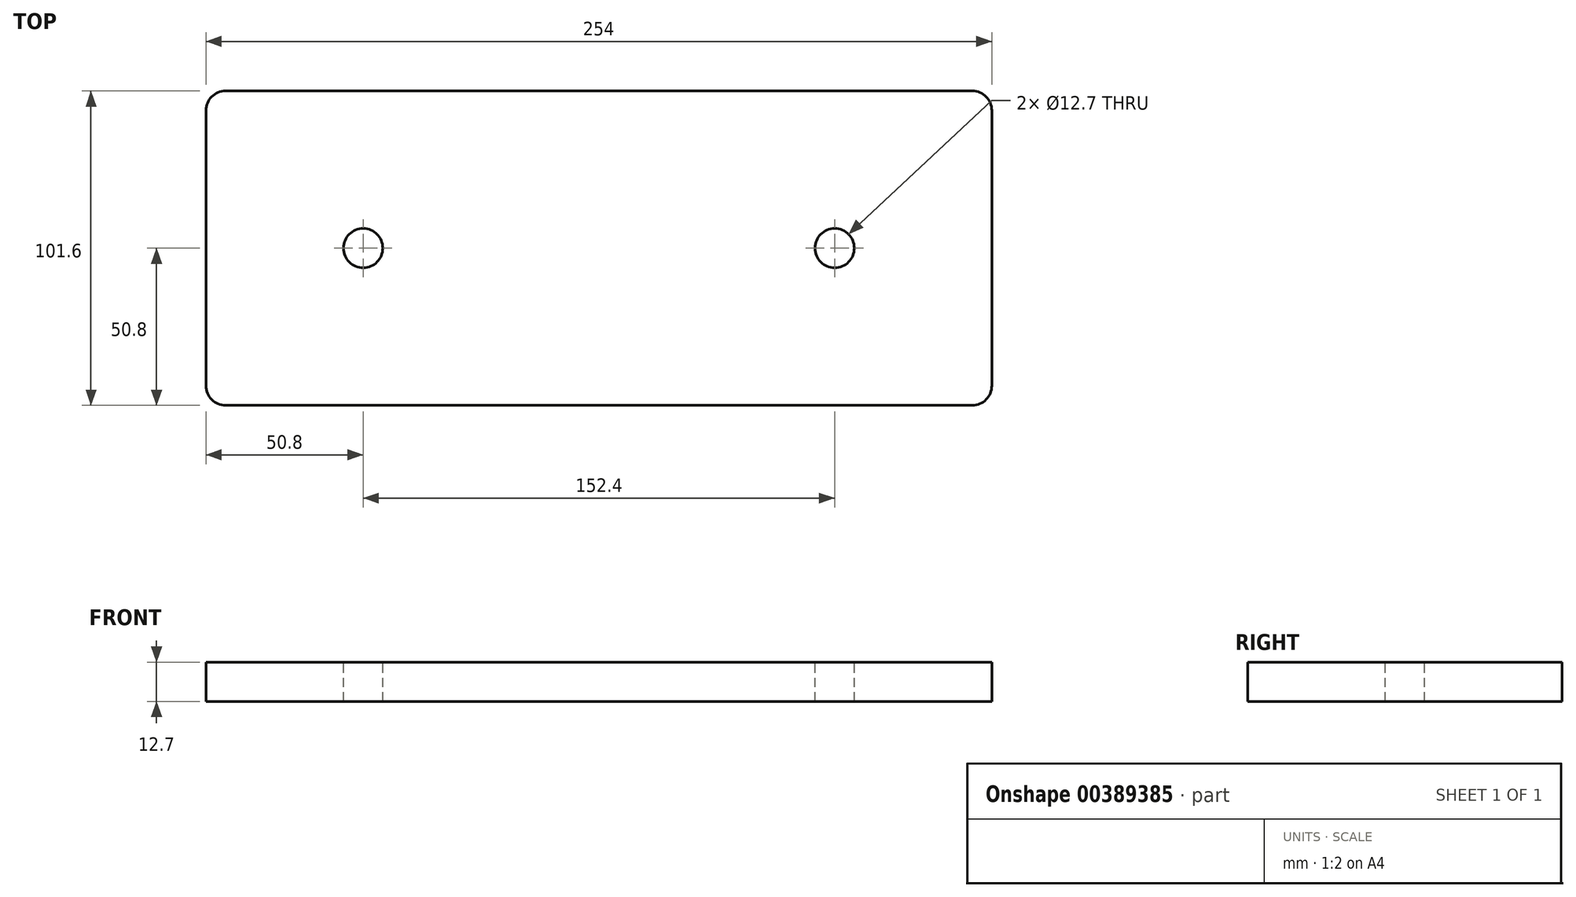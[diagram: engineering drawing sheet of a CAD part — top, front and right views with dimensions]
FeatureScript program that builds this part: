
annotation { "Feature Type Name" : "Feature", "Feature Type Description" : "" }
export const myFeature = defineFeature(function(context is Context, id is Id, definition is map)
    precondition{}
    {
        {
            var Q0;
            Q0=qCreatedBy(makeId("Top.planeOp"),FACE);
            var sketch = newSketch(context, id + "F0", { "sketchPlane" : qUnion([Q0])});
            skLineSegment(sketch, "E0.bottom", {"start": v(6.35, 0) * mm, "end": v(247.65, 0) * mm});
            skLineSegment(sketch, "E0.top", {"start": v(6.35, 101.6) * mm, "end": v(247.65, 101.6) * mm});
            skLineSegment(sketch, "E0.left", {"start": v(0, 6.35) * mm, "end": v(0, 95.25) * mm});
            skLineSegment(sketch, "E0.right", {"start": v(254, 6.35) * mm, "end": v(254, 95.25) * mm});
            skPoint(sketch, "E1.visualSharp", {"position": v(0, 101.6) * mm});
            skArc(sketch, "E1.filletArc", {"start": v(6.35, 101.6) * mm, "mid": v(1.86, 99.74) * mm, "end": v(0, 95.25) * mm});
            skPoint(sketch, "E2.visualSharp", {"position": v(0, 0) * mm});
            skArc(sketch, "E2.filletArc", {"start": v(0, 6.35) * mm, "mid": v(1.86, 1.86) * mm, "end": v(6.35, 0) * mm});
            skPoint(sketch, "E3.visualSharp", {"position": v(254, 0) * mm});
            skArc(sketch, "E3.filletArc", {"start": v(247.65, 0) * mm, "mid": v(252.14, 1.86) * mm, "end": v(254, 6.35) * mm});
            skPoint(sketch, "E4.visualSharp", {"position": v(254, 101.6) * mm});
            skArc(sketch, "E4.filletArc", {"start": v(254, 95.25) * mm, "mid": v(252.14, 99.74) * mm, "end": v(247.65, 101.6) * mm});
            skSolve(sketch);
        }
        {
            var Q0;
            Q0 = qSketchRegion(id + "F0", true);
            extrude(context, id + "F1", {"entities" : qUnion([Q0]), "depth" : 12.7 * mm});
        }
        {
            var Q0;
            Q0=makeQuery(id+"F1.opExtrude","CAP_FACE",FACE,{"disambiguationData":[OSD([sQuery(id+"F0.wireOp",EDGE,"E0.bottom"),sQuery(id+"F0.wireOp",EDGE,"E0.top"),sQuery(id+"F0.wireOp",EDGE,"E0.left"),sQuery(id+"F0.wireOp",EDGE,"E0.right"),sQuery(id+"F0.wireOp",EDGE,"E1.filletArc"),sQuery(id+"F0.wireOp",EDGE,"E2.filletArc"),sQuery(id+"F0.wireOp",EDGE,"E3.filletArc"),sQuery(id+"F0.wireOp",EDGE,"E4.filletArc")])],"isStart":false});
            var sketch = newSketch(context, id + "F2", { "sketchPlane" : qUnion([Q0])});
            skCircle(sketch, "E5", {"center": v(50.8, 50.8) * mm, "radius": 6.35 * mm});
            skPoint(sketch, "E5.centerSnap0", {"position": v(0, 50.8) * mm});
            skCircle(sketch, "E6", {"center": v(203.2, 50.8) * mm, "radius": 6.35 * mm});
            skSolve(sketch);
        }
        {
            var Q0;
            Q0 = qSketchRegion(id + "F2", true);
            extrude(context, id + "F3", {"entities" : qUnion([Q0]), "operationType" : NewBodyOperationType.REMOVE, "endBound" : BoundingType.THROUGH_ALL, "oppositeDirection" : true, "depth" : 25.4 * mm});
        }
    });
